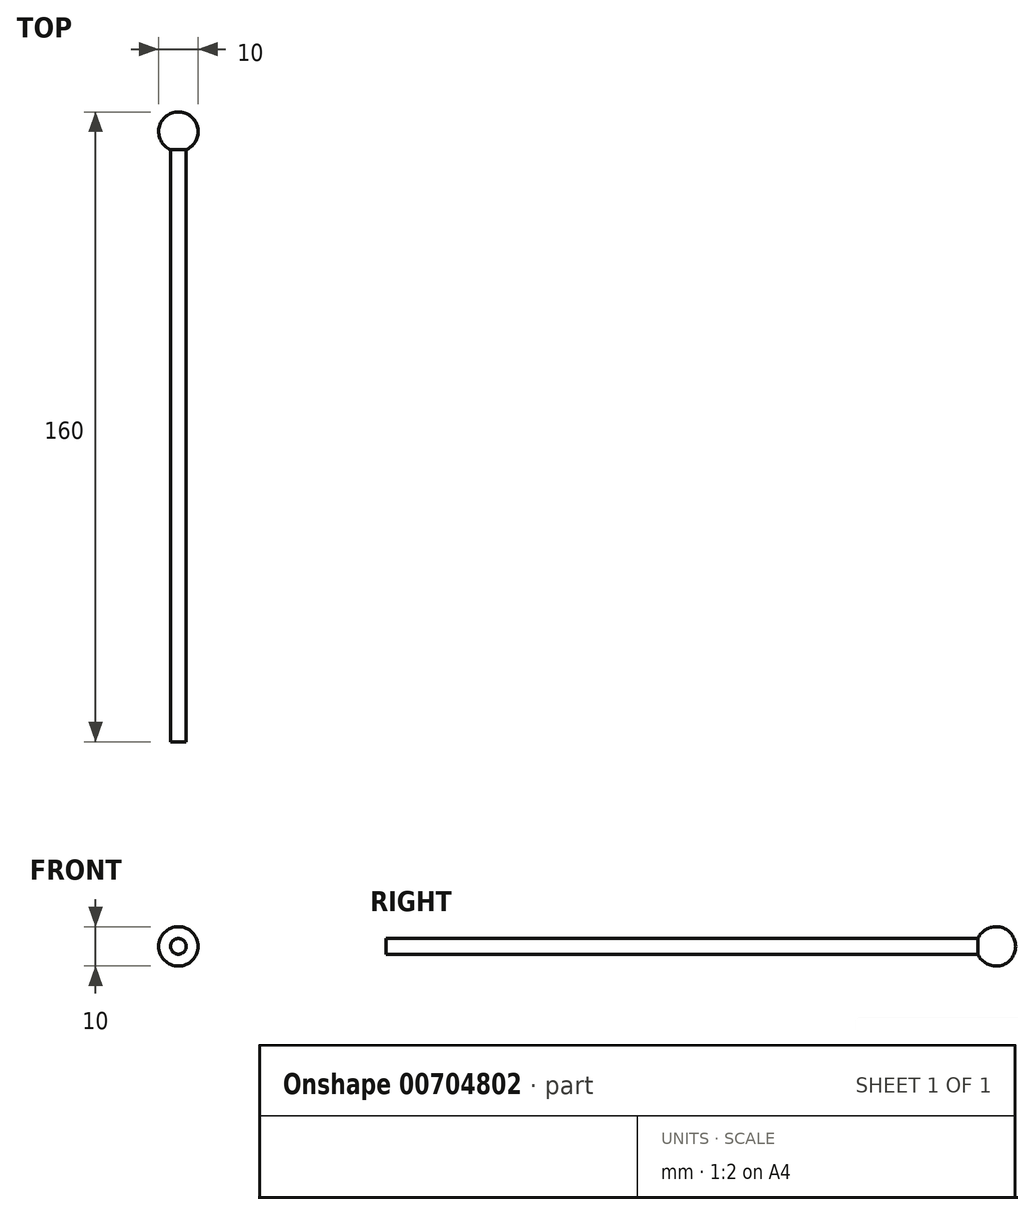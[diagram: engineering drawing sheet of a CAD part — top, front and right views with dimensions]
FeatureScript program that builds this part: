
annotation { "Feature Type Name" : "Feature", "Feature Type Description" : "" }
export const myFeature = defineFeature(function(context is Context, id is Id, definition is map)
    precondition{}
    {
        {
            var Q0;
            Q0=qCreatedBy(makeId("Top.planeOp"),FACE);
            var sketch = newSketch(context, id + "F0", { "sketchPlane" : qUnion([Q0])});
            skLineSegment(sketch, "E0", {"start": v(2, -40.96) * mm, "end": v(2, 109.04) * mm});
            skLineSegment(sketch, "E1", {"start": v(2, -40.96) * mm, "end": v(4, -40.96) * mm});
            skArc(sketch, "E2", {"start": v(4, 109.46) * mm, "mid": v(6.9, 115.07) * mm, "end": v(2, 119.04) * mm});
            skLineSegment(sketch, "E3", {"start": v(2, 109.04) * mm, "end": v(2, 119.04) * mm});
            skLineSegment(sketch, "E4", {"start": v(4, -40.96) * mm, "end": v(4, 109.46) * mm});
            skSolve(sketch);
        }
        {
            var Q0;
            Q0=makeQuery(id+"F0.imprint","IMPRINT",FACE,{"disambiguationData":[TD([[makeQuery(id+"F0.imprint","IMPRINT",EDGE,{"derivedFrom":sQuery(id+"F0.wireOp",EDGE,"E0")}),-1.0]])]});
            var Q1;
            Q1=sQuery(id+"F0.wireOp",EDGE,"E0");
            revolve(context, id + "F1", {"surfaceOperationType" : NewSurfaceOperationType.NEW, "entities" : qUnion([Q0]), "axis" : qUnion([Q1]), "revolveType" : RevolveType.FULL});
        }
    });
